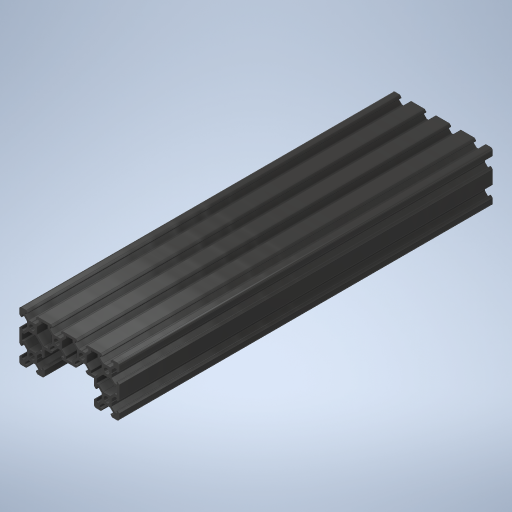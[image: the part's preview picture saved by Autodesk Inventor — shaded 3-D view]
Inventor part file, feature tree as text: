
AUTODESK INVENTOR PART (.ipt)
format: ipt  version: 2024.2 (Build 282272000, 272)  size: 564,224 bytes
history: native  units: mm
features: extrude x1, sketch x1
ambient origin geometry x8: Origin, YZ Plane, XZ Plane, XY Plane, X Axis, Y Axis, Z Axis, Center Point
bodies: Solid1 (feature_tree)
feature tree (2):
  extrude  "Extrusion1"  [1 undecoded]
  sketch  "Sketch1"  dims[d0=300.0mm d1=0.0mm]
note: 1 required parameter value undecoded (feature->parameter linkage not recoverable at this tier; creation-order binding heuristic only, values carry confidence <= 0.55)
